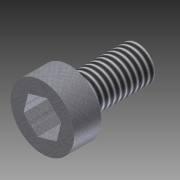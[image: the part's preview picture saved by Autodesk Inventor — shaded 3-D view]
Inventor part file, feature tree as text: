
AUTODESK INVENTOR PART (.ipt)
format: ipt  version: 2012 (Build 160160000, 160)  size: 115,200 bytes
history: native  units: in
note: dims shown in document units (in); Inventor stores cm internally (conversion verified against a paired STEP export)
features: extrude x2, sketch x1, thread x1
ambient origin geometry x8: Origin, YZ Plane, XZ Plane, XY Plane, X Axis, Y Axis, Z Axis, Center Point
bodies: Solid1 (feature_tree)
feature tree (4):
  sketch  "Sketch1"  dims[d0=0.19in d1=0.35in d2=0.375in d3=0.0in d4=0.15in d5=0.0in d6=1.0in d7=0.0in]
  extrude  "Extrusion1"  Depth=0.35in
  extrude  "Extrusion2"  Depth=0.375in TaperAngle=0.0deg
  thread  "Thread1"  [1 undecoded]
note: 1 required parameter value undecoded (feature->parameter linkage not recoverable at this tier; creation-order binding heuristic only, values carry confidence <= 0.55)
